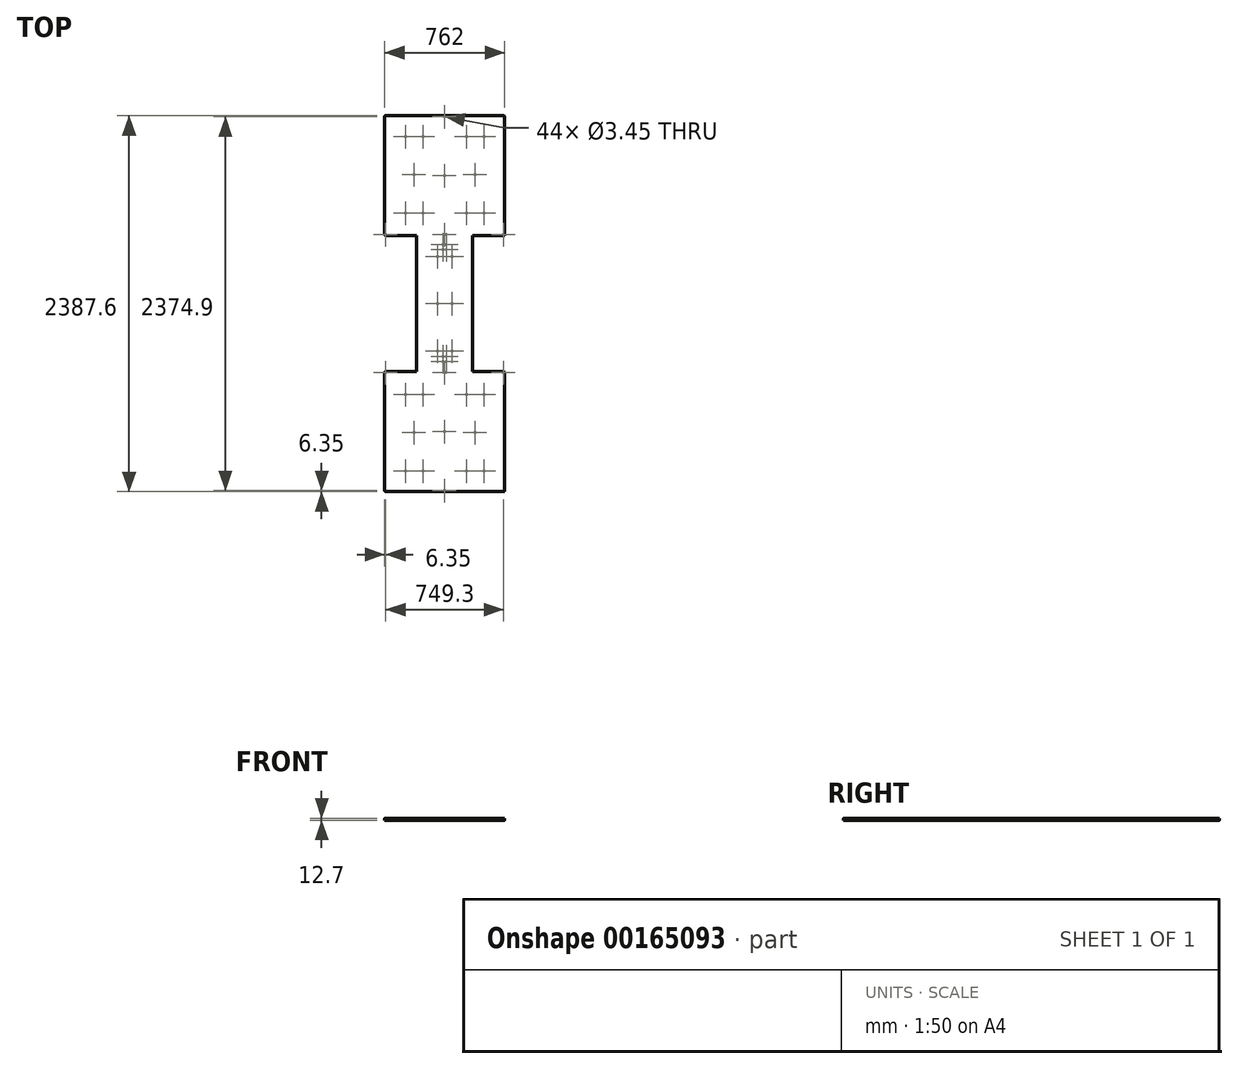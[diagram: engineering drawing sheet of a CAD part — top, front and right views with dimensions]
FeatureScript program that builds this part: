
annotation { "Feature Type Name" : "Feature", "Feature Type Description" : "" }
export const myFeature = defineFeature(function(context is Context, id is Id, definition is map)
    precondition{}
    {
        {
            var Q0;
            Q0=qCreatedBy(makeId("Top.planeOp"),FACE);
            var sketch = newSketch(context, id + "F0", { "sketchPlane" : qUnion([Q0])});
            skLineSegment(sketch, "E0", {"start": v(-177.8, 0) * mm, "end": v(177.8, 0) * mm, "construction": true});
            skLineSegment(sketch, "E1.left", {"start": v(-177.8, -431.8) * mm, "end": v(-177.8, 431.8) * mm});
            skLineSegment(sketch, "E1.right", {"start": v(177.8, -431.8) * mm, "end": v(177.8, 431.8) * mm});
            skLineSegment(sketch, "E2.bottom", {"start": v(-177.8, 431.8) * mm, "end": v(-381, 431.8) * mm});
            skLineSegment(sketch, "E2.top", {"start": v(381, 1193.8) * mm, "end": v(-381, 1193.8) * mm});
            skLineSegment(sketch, "E2.left", {"start": v(381, 431.8) * mm, "end": v(381, 1193.8) * mm});
            skLineSegment(sketch, "E2.right", {"start": v(-381, 431.8) * mm, "end": v(-381, 1193.8) * mm});
            skLineSegment(sketch, "E3", {"start": v(0, 0) * mm, "end": v(0, 1193.8) * mm, "construction": true});
            skLineSegment(sketch, "E4", {"start": v(-177.8, -431.8) * mm, "end": v(-381, -431.8) * mm});
            skLineSegment(sketch, "E5", {"start": v(177.8, 431.8) * mm, "end": v(381, 431.8) * mm});
            skLineSegment(sketch, "E6.bottom", {"start": v(381, -1193.8) * mm, "end": v(-381, -1193.8) * mm});
            skLineSegment(sketch, "E6.top", {"start": v(381, -431.8) * mm, "end": v(177.8, -431.8) * mm});
            skLineSegment(sketch, "E6.left", {"start": v(381, -1193.8) * mm, "end": v(381, -431.8) * mm});
            skLineSegment(sketch, "E6.right", {"start": v(-381, -1193.8) * mm, "end": v(-381, -431.8) * mm});
            skLineSegment(sketch, "E7", {"start": v(0, 0) * mm, "end": v(0, -1193.8) * mm, "construction": true});
            skLineSegment(sketch, "E8.bottom", {"start": v(-46.04, -300.04) * mm, "end": v(46.04, -300.04) * mm, "construction": true});
            skLineSegment(sketch, "E8.top", {"start": v(-46.04, 300.04) * mm, "end": v(46.04, 300.04) * mm, "construction": true});
            skLineSegment(sketch, "E8.left", {"start": v(-46.04, -300.04) * mm, "end": v(-46.04, 300.04) * mm, "construction": true});
            skLineSegment(sketch, "E8.right", {"start": v(46.04, -300.04) * mm, "end": v(46.04, 300.04) * mm, "construction": true});
            skPoint(sketch, "E8.middle", {"position": v(0, 0) * mm});
            skCircle(sketch, "E9", {"center": v(-46.04, 300.04) * mm, "radius": 1.73 * mm});
            skCircle(sketch, "E10", {"center": v(46.04, 300.04) * mm, "radius": 1.73 * mm});
            skCircle(sketch, "E11", {"center": v(46.04, 0) * mm, "radius": 1.73 * mm});
            skCircle(sketch, "E12", {"center": v(-46.04, 0) * mm, "radius": 1.73 * mm});
            skCircle(sketch, "E13", {"center": v(-46.04, -300.04) * mm, "radius": 1.73 * mm});
            skCircle(sketch, "E14", {"center": v(46.04, -300.04) * mm, "radius": 1.73 * mm});
            skLineSegment(sketch, "E15", {"start": v(193.67, 1193.8) * mm, "end": v(193.68, 819.15) * mm, "construction": true});
            skLineSegment(sketch, "E16", {"start": v(193.67, 819.15) * mm, "end": v(381, 819.15) * mm, "construction": true});
            skLineSegment(sketch, "E17", {"start": v(-193.67, 1193.8) * mm, "end": v(-193.67, 819.15) * mm, "construction": true});
            skLineSegment(sketch, "E18", {"start": v(-193.67, 819.15) * mm, "end": v(-381, 819.15) * mm, "construction": true});
            skLineSegment(sketch, "E19.bottom", {"start": v(249.24, 1062.04) * mm, "end": v(138.11, 1062.04) * mm, "construction": true});
            skLineSegment(sketch, "E19.top", {"start": v(249.24, 576.26) * mm, "end": v(138.11, 576.26) * mm, "construction": true});
            skLineSegment(sketch, "E19.left", {"start": v(249.24, 1062.04) * mm, "end": v(249.24, 576.26) * mm, "construction": true});
            skLineSegment(sketch, "E19.right", {"start": v(138.11, 1062.04) * mm, "end": v(138.11, 576.26) * mm, "construction": true});
            skPoint(sketch, "E19.middle", {"position": v(193.67, 819.15) * mm});
            skCircle(sketch, "E20", {"center": v(138.11, 1062.04) * mm, "radius": 1.73 * mm});
            skCircle(sketch, "E21", {"center": v(249.24, 1062.04) * mm, "radius": 1.73 * mm});
            skCircle(sketch, "E22", {"center": v(138.11, 576.26) * mm, "radius": 1.73 * mm});
            skCircle(sketch, "E23", {"center": v(249.24, 576.26) * mm, "radius": 1.73 * mm});
            skCircle(sketch, "E24", {"center": v(193.67, 819.15) * mm, "radius": 1.73 * mm});
            skLineSegment(sketch, "E25.bottom", {"start": v(-138.11, 1062.04) * mm, "end": v(-249.24, 1062.04) * mm, "construction": true});
            skLineSegment(sketch, "E25.top", {"start": v(-138.11, 576.26) * mm, "end": v(-249.24, 576.26) * mm, "construction": true});
            skLineSegment(sketch, "E25.left", {"start": v(-138.11, 1062.04) * mm, "end": v(-138.11, 576.26) * mm, "construction": true});
            skLineSegment(sketch, "E25.right", {"start": v(-249.24, 1062.04) * mm, "end": v(-249.24, 576.26) * mm, "construction": true});
            skPoint(sketch, "E25.middle", {"position": v(-193.67, 819.15) * mm});
            skCircle(sketch, "E26", {"center": v(-249.24, 1062.04) * mm, "radius": 1.73 * mm});
            skCircle(sketch, "E27", {"center": v(-138.11, 1062.04) * mm, "radius": 1.73 * mm});
            skCircle(sketch, "E28", {"center": v(-193.67, 819.15) * mm, "radius": 1.73 * mm});
            skCircle(sketch, "E29", {"center": v(-138.11, 576.26) * mm, "radius": 1.73 * mm});
            skCircle(sketch, "E30", {"center": v(-249.24, 576.26) * mm, "radius": 1.73 * mm});
            skLineSegment(sketch, "E31", {"start": v(-193.67, -1193.8) * mm, "end": v(-193.67, -819.15) * mm, "construction": true});
            skLineSegment(sketch, "E32", {"start": v(-193.67, -819.15) * mm, "end": v(-381, -819.15) * mm, "construction": true});
            skLineSegment(sketch, "E33", {"start": v(193.67, -1193.8) * mm, "end": v(193.67, -819.15) * mm, "construction": true});
            skLineSegment(sketch, "E34", {"start": v(193.67, -819.15) * mm, "end": v(381, -819.15) * mm, "construction": true});
            skLineSegment(sketch, "E35.bottom", {"start": v(-138.11, -576.26) * mm, "end": v(-249.24, -576.26) * mm, "construction": true});
            skLineSegment(sketch, "E35.top", {"start": v(-138.11, -1062.04) * mm, "end": v(-249.24, -1062.04) * mm, "construction": true});
            skLineSegment(sketch, "E35.left", {"start": v(-138.11, -576.26) * mm, "end": v(-138.11, -1062.04) * mm, "construction": true});
            skLineSegment(sketch, "E35.right", {"start": v(-249.24, -576.26) * mm, "end": v(-249.24, -1062.04) * mm, "construction": true});
            skPoint(sketch, "E35.middle", {"position": v(-193.67, -819.15) * mm});
            skLineSegment(sketch, "E36.bottom", {"start": v(138.11, -576.26) * mm, "end": v(249.24, -576.26) * mm, "construction": true});
            skLineSegment(sketch, "E36.top", {"start": v(138.11, -1062.04) * mm, "end": v(249.24, -1062.04) * mm, "construction": true});
            skLineSegment(sketch, "E36.left", {"start": v(138.11, -576.26) * mm, "end": v(138.11, -1062.04) * mm, "construction": true});
            skLineSegment(sketch, "E36.right", {"start": v(249.24, -576.26) * mm, "end": v(249.24, -1062.04) * mm, "construction": true});
            skPoint(sketch, "E36.middle", {"position": v(193.67, -819.15) * mm});
            skCircle(sketch, "E37", {"center": v(-249.24, -576.26) * mm, "radius": 1.73 * mm});
            skCircle(sketch, "E38", {"center": v(-138.11, -576.26) * mm, "radius": 1.73 * mm});
            skCircle(sketch, "E39", {"center": v(-193.67, -819.15) * mm, "radius": 1.73 * mm});
            skCircle(sketch, "E40", {"center": v(-138.11, -1062.04) * mm, "radius": 1.73 * mm});
            skCircle(sketch, "E41", {"center": v(-249.24, -1062.04) * mm, "radius": 1.73 * mm});
            skCircle(sketch, "E42", {"center": v(138.11, -1062.04) * mm, "radius": 1.73 * mm});
            skCircle(sketch, "E43", {"center": v(249.24, -1062.04) * mm, "radius": 1.73 * mm});
            skCircle(sketch, "E44", {"center": v(193.67, -819.15) * mm, "radius": 1.73 * mm});
            skCircle(sketch, "E45", {"center": v(138.11, -576.26) * mm, "radius": 1.73 * mm});
            skCircle(sketch, "E46", {"center": v(249.24, -576.26) * mm, "radius": 1.73 * mm});
            skSolve(sketch);
        }
        {
            var Q0;
            Q0 = qSketchRegion(id + "F0", true);
            extrude(context, id + "F1", {"entities" : qUnion([Q0]), "depth" : 12.7 * mm});
        }
        {
            var Q0;
            Q0=makeQuery(id+"F1.opExtrude","CAP_FACE",FACE,{"disambiguationData":[OSD([sQuery(id+"F0.wireOp",EDGE,"E1.left"),sQuery(id+"F0.wireOp",EDGE,"E1.right"),sQuery(id+"F0.wireOp",EDGE,"E2.bottom"),sQuery(id+"F0.wireOp",EDGE,"E2.top"),sQuery(id+"F0.wireOp",EDGE,"E2.left"),sQuery(id+"F0.wireOp",EDGE,"E2.right"),sQuery(id+"F0.wireOp",EDGE,"E4"),sQuery(id+"F0.wireOp",EDGE,"E5"),sQuery(id+"F0.wireOp",EDGE,"E6.bottom"),sQuery(id+"F0.wireOp",EDGE,"E6.top"),sQuery(id+"F0.wireOp",EDGE,"E6.left"),sQuery(id+"F0.wireOp",EDGE,"E6.right")])],"isStart":false});
            var sketch = newSketch(context, id + "F2", { "sketchPlane" : qUnion([Q0])});
            skLineSegment(sketch, "E47.bottom", {"start": v(-381, -431.8) * mm, "end": v(-374.65, -431.8) * mm, "construction": true});
            skLineSegment(sketch, "E47.top", {"start": v(-381, -438.15) * mm, "end": v(-374.65, -438.15) * mm, "construction": true});
            skLineSegment(sketch, "E47.left", {"start": v(-381, -431.8) * mm, "end": v(-381, -438.15) * mm, "construction": true});
            skLineSegment(sketch, "E47.right", {"start": v(-374.65, -431.8) * mm, "end": v(-374.65, -438.15) * mm, "construction": true});
            skLineSegment(sketch, "E48.bottom", {"start": v(381, -431.8) * mm, "end": v(374.65, -431.8) * mm, "construction": true});
            skLineSegment(sketch, "E48.top", {"start": v(381, -438.15) * mm, "end": v(374.65, -438.15) * mm, "construction": true});
            skLineSegment(sketch, "E48.left", {"start": v(381, -431.8) * mm, "end": v(381, -438.15) * mm, "construction": true});
            skLineSegment(sketch, "E48.right", {"start": v(374.65, -431.8) * mm, "end": v(374.65, -438.15) * mm, "construction": true});
            skLineSegment(sketch, "E49", {"start": v(177.8, -431.8) * mm, "end": v(-177.8, -431.8) * mm, "construction": true});
            skLineSegment(sketch, "E50", {"start": v(0, -431.8) * mm, "end": v(0, -438.15) * mm, "construction": true});
            skLineSegment(sketch, "E51", {"start": v(0, -1193.8) * mm, "end": v(0, -1187.45) * mm, "construction": true});
            skCircle(sketch, "E52", {"center": v(0, -438.15) * mm, "radius": 1.73 * mm});
            skCircle(sketch, "E53", {"center": v(-374.65, -438.15) * mm, "radius": 1.73 * mm});
            skCircle(sketch, "E54", {"center": v(374.65, -438.15) * mm, "radius": 1.73 * mm});
            skCircle(sketch, "E55", {"center": v(0, -1187.45) * mm, "radius": 1.73 * mm});
            skLineSegment(sketch, "E56", {"start": v(0, -1187.45) * mm, "end": v(0, -438.15) * mm, "construction": true});
            skCircle(sketch, "E57", {"center": v(0, -812.8) * mm, "radius": 1.73 * mm});
            skLineSegment(sketch, "E58", {"start": v(177.8, 431.8) * mm, "end": v(-177.8, 431.8) * mm, "construction": true});
            skLineSegment(sketch, "E59", {"start": v(0, 431.8) * mm, "end": v(0, 438.15) * mm, "construction": true});
            skLineSegment(sketch, "E60", {"start": v(0, 438.15) * mm, "end": v(0, 1187.45) * mm, "construction": true});
            skLineSegment(sketch, "E61", {"start": v(0, 1187.45) * mm, "end": v(0, 1193.8) * mm, "construction": true});
            skLineSegment(sketch, "E62.bottom", {"start": v(381, 431.8) * mm, "end": v(374.65, 431.8) * mm, "construction": true});
            skLineSegment(sketch, "E62.top", {"start": v(381, 438.15) * mm, "end": v(374.65, 438.15) * mm, "construction": true});
            skLineSegment(sketch, "E62.left", {"start": v(381, 431.8) * mm, "end": v(381, 438.15) * mm, "construction": true});
            skLineSegment(sketch, "E62.right", {"start": v(374.65, 431.8) * mm, "end": v(374.65, 438.15) * mm, "construction": true});
            skLineSegment(sketch, "E63.bottom", {"start": v(-381, 431.8) * mm, "end": v(-374.65, 431.8) * mm, "construction": true});
            skLineSegment(sketch, "E63.top", {"start": v(-381, 438.15) * mm, "end": v(-374.65, 438.15) * mm, "construction": true});
            skLineSegment(sketch, "E63.left", {"start": v(-381, 431.8) * mm, "end": v(-381, 438.15) * mm, "construction": true});
            skLineSegment(sketch, "E63.right", {"start": v(-374.65, 431.8) * mm, "end": v(-374.65, 438.15) * mm, "construction": true});
            skCircle(sketch, "E64", {"center": v(374.65, 438.15) * mm, "radius": 1.73 * mm});
            skCircle(sketch, "E65", {"center": v(0, 438.15) * mm, "radius": 1.73 * mm});
            skCircle(sketch, "E66", {"center": v(0, 812.8) * mm, "radius": 1.73 * mm});
            skCircle(sketch, "E67", {"center": v(0, 1187.45) * mm, "radius": 1.73 * mm});
            skCircle(sketch, "E68", {"center": v(-374.65, 438.15) * mm, "radius": 1.73 * mm});
            skLineSegment(sketch, "E69", {"start": v(0, 438.15) * mm, "end": v(0, 358.78) * mm, "construction": true});
            skLineSegment(sketch, "E70", {"start": v(0, 358.78) * mm, "end": v(0, -352.43) * mm, "construction": true});
            skLineSegment(sketch, "E71", {"start": v(0, -352.43) * mm, "end": v(0, -431.8) * mm, "construction": true});
            skLineSegment(sketch, "E72.bottom", {"start": v(10.32, 374.65) * mm, "end": v(-10.32, 374.65) * mm, "construction": true});
            skLineSegment(sketch, "E72.top", {"start": v(10.32, 342.9) * mm, "end": v(-10.32, 342.9) * mm, "construction": true});
            skLineSegment(sketch, "E72.left", {"start": v(10.32, 374.65) * mm, "end": v(10.32, 342.9) * mm, "construction": true});
            skLineSegment(sketch, "E72.right", {"start": v(-10.32, 374.65) * mm, "end": v(-10.32, 342.9) * mm, "construction": true});
            skPoint(sketch, "E72.middle", {"position": v(0, 358.78) * mm});
            skCircle(sketch, "E73", {"center": v(-10.32, 374.65) * mm, "radius": 1.73 * mm});
            skCircle(sketch, "E74", {"center": v(-10.32, 342.9) * mm, "radius": 1.73 * mm});
            skCircle(sketch, "E75", {"center": v(10.32, 342.9) * mm, "radius": 1.73 * mm});
            skCircle(sketch, "E76", {"center": v(10.32, 374.65) * mm, "radius": 1.73 * mm});
            skLineSegment(sketch, "E77.bottom", {"start": v(10.32, -336.55) * mm, "end": v(-10.32, -336.55) * mm, "construction": true});
            skLineSegment(sketch, "E77.top", {"start": v(10.32, -368.3) * mm, "end": v(-10.32, -368.3) * mm, "construction": true});
            skLineSegment(sketch, "E77.left", {"start": v(10.32, -336.55) * mm, "end": v(10.32, -368.3) * mm, "construction": true});
            skLineSegment(sketch, "E77.right", {"start": v(-10.32, -336.55) * mm, "end": v(-10.32, -368.3) * mm, "construction": true});
            skPoint(sketch, "E77.middle", {"position": v(0, -352.43) * mm});
            skCircle(sketch, "E78", {"center": v(-10.32, -336.55) * mm, "radius": 1.73 * mm});
            skCircle(sketch, "E79", {"center": v(10.32, -336.55) * mm, "radius": 1.73 * mm});
            skCircle(sketch, "E80", {"center": v(10.32, -368.3) * mm, "radius": 1.73 * mm});
            skCircle(sketch, "E81", {"center": v(-10.32, -368.3) * mm, "radius": 1.73 * mm});
            skSolve(sketch);
        }
        {
            var Q0;
            Q0 = qSketchRegion(id + "F2", true);
            var Q1;
            Q1=makeQuery(id+"F1.opExtrude","CAP_FACE",FACE,{"disambiguationData":[OSD([sQuery(id+"F0.wireOp",EDGE,"E1.left"),sQuery(id+"F0.wireOp",EDGE,"E1.right"),sQuery(id+"F0.wireOp",EDGE,"E2.bottom"),sQuery(id+"F0.wireOp",EDGE,"E2.top"),sQuery(id+"F0.wireOp",EDGE,"E2.left"),sQuery(id+"F0.wireOp",EDGE,"E2.right"),sQuery(id+"F0.wireOp",EDGE,"E4"),sQuery(id+"F0.wireOp",EDGE,"E5"),sQuery(id+"F0.wireOp",EDGE,"E6.bottom"),sQuery(id+"F0.wireOp",EDGE,"E6.top"),sQuery(id+"F0.wireOp",EDGE,"E6.left"),sQuery(id+"F0.wireOp",EDGE,"E6.right")])],"isStart":true});
            extrude(context, id + "F3", {"entities" : qUnion([Q0]), "operationType" : NewBodyOperationType.REMOVE, "endBound" : BoundingType.UP_TO_SURFACE, "oppositeDirection" : true, "endBoundEntityFace" : qUnion([Q1]), "depth" : 25.4 * mm});
        }
        {
            var Q0;
            Q0=makeQuery(id+"F1.opExtrude","SWEPT_EDGE",EDGE,{"disambiguationData":[OSD([sQuery(id+"F0.wireOp",EDGE,"E4"),sQuery(id+"F0.wireOp",EDGE,"E6.right")])]});
            var Q1;
            Q1=makeQuery(id+"F1.opExtrude","SWEPT_EDGE",EDGE,{"disambiguationData":[OSD([sQuery(id+"F0.wireOp",EDGE,"E6.top"),sQuery(id+"F0.wireOp",EDGE,"E6.left")])]});
            var Q2;
            Q2=makeQuery(id+"F1.opExtrude","SWEPT_EDGE",EDGE,{"disambiguationData":[OSD([sQuery(id+"F0.wireOp",EDGE,"E6.bottom"),sQuery(id+"F0.wireOp",EDGE,"E6.left")])]});
            var Q3;
            Q3=makeQuery(id+"F1.opExtrude","SWEPT_EDGE",EDGE,{"disambiguationData":[OSD([sQuery(id+"F0.wireOp",EDGE,"E6.bottom"),sQuery(id+"F0.wireOp",EDGE,"E6.right")])]});
            var Q4;
            Q4=makeQuery(id+"F1.opExtrude","SWEPT_EDGE",EDGE,{"disambiguationData":[OSD([sQuery(id+"F0.wireOp",EDGE,"E2.bottom"),sQuery(id+"F0.wireOp",EDGE,"E2.right")])]});
            var Q5;
            Q5=makeQuery(id+"F1.opExtrude","SWEPT_EDGE",EDGE,{"disambiguationData":[OSD([sQuery(id+"F0.wireOp",EDGE,"E2.left"),sQuery(id+"F0.wireOp",EDGE,"E5")])]});
            var Q6;
            Q6=makeQuery(id+"F1.opExtrude","SWEPT_EDGE",EDGE,{"disambiguationData":[OSD([sQuery(id+"F0.wireOp",EDGE,"E2.top"),sQuery(id+"F0.wireOp",EDGE,"E2.left")])]});
            var Q7;
            Q7=makeQuery(id+"F1.opExtrude","SWEPT_EDGE",EDGE,{"disambiguationData":[OSD([sQuery(id+"F0.wireOp",EDGE,"E2.top"),sQuery(id+"F0.wireOp",EDGE,"E2.right")])]});
            fillet(context, id + "F4", {"entities" : qUnion([Q0, Q1, Q2, Q3, Q4, Q5, Q6, Q7]), "radius" : 6.35 * mm, "tangentPropagation" : true, "allowEdgeOverflow" : false});
        }
    });
